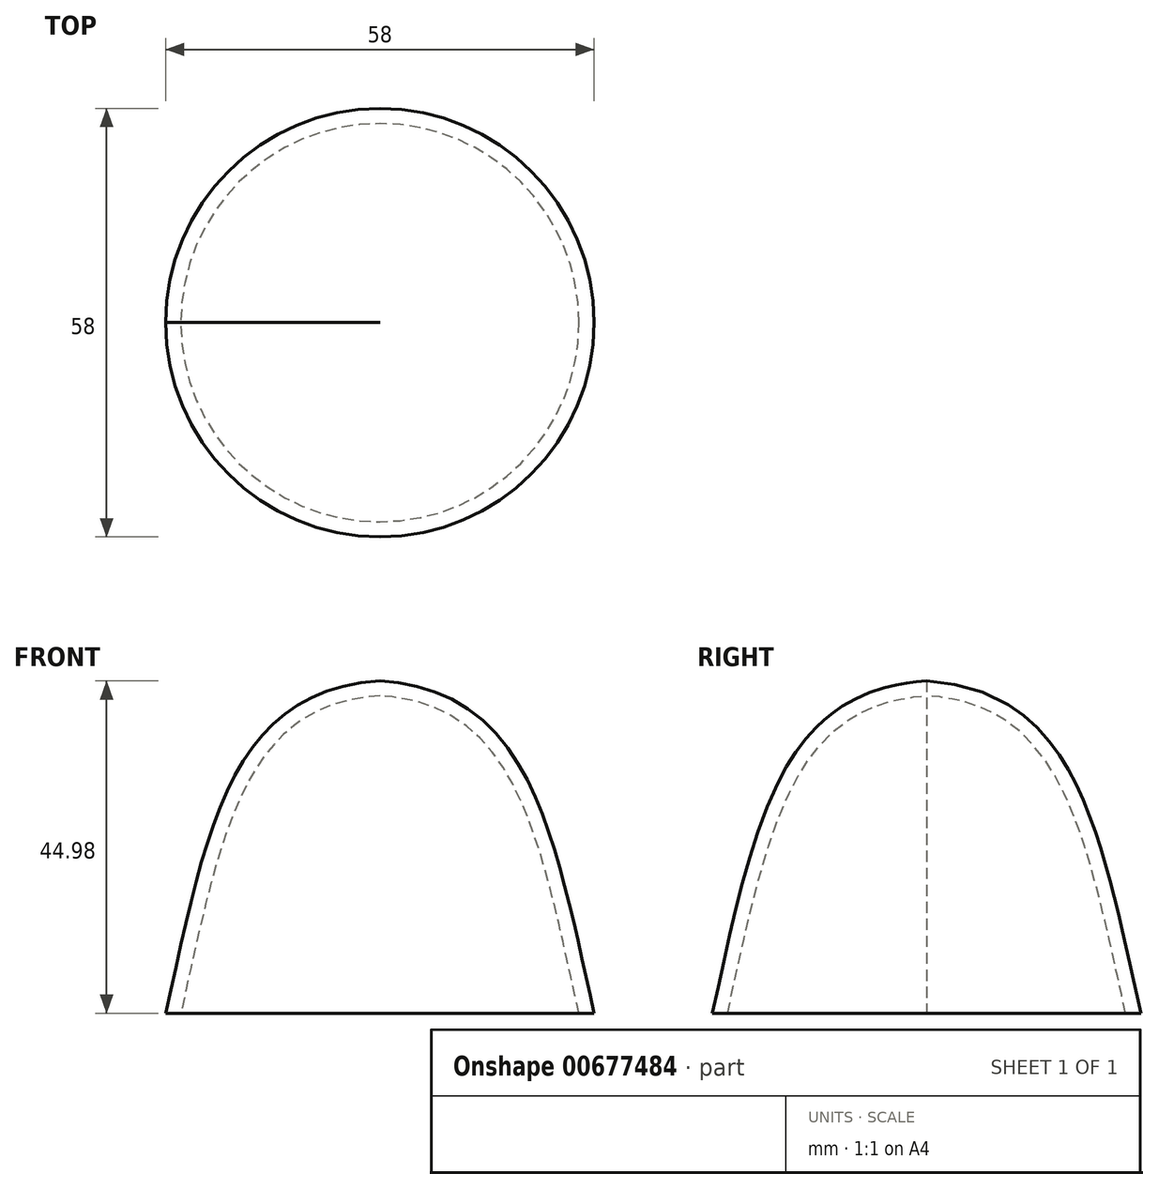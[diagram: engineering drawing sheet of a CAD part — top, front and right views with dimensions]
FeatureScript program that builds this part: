
annotation { "Feature Type Name" : "Feature", "Feature Type Description" : "" }
export const myFeature = defineFeature(function(context is Context, id is Id, definition is map)
    precondition{}
    {
        {
            var Q0;
            Q0=qCreatedBy(makeId("Front.planeOp"),FACE);
            var sketch = newSketch(context, id + "F0", { "sketchPlane" : qUnion([Q0])});
            skLineSegment(sketch, "E0", {"start": v(0, 0) * mm, "end": v(0, 45) * mm});
            skLineSegment(sketch, "E1", {"start": v(-29, 0.02) * mm, "end": v(0, 0) * mm});
            skFitSpline(sketch, "E2", {"points": [v(0, 45) * mm, v(-29, 0.02) * mm], "startDerivative": vector(-61.69, -3.83) * mm, "endDerivative": vector(-16.4, -72.98) * mm});
            skSolve(sketch);
        }
        {
            var Q0;
            Q0=makeQuery(id+"F0.imprint","IMPRINT",FACE,{"disambiguationData":[TD([[makeQuery(id+"F0.imprint","IMPRINT",EDGE,{"derivedFrom":sQuery(id+"F0.wireOp",EDGE,"E0")}),1.0]])]});
            var Q1;
            Q1=sQuery(id+"F0.wireOp",EDGE,"E0");
            var Q2;
            Q2=sQuery(id+"F0.wireOp",EDGE,"E1");
            var Q3;
            Q3=sQuery(id+"F0.wireOp",EDGE,"E2");
            var Q4;
            Q4=sQuery(id+"F0.wireOp",EDGE,"E0");
            revolve(context, id + "F1", {"entities" : qUnion([Q0]), "surfaceEntities" : qUnion([Q1, Q2, Q3]), "axis" : qUnion([Q4]), "revolveType" : RevolveType.FULL});
        }
        {
            var Q0;
            Q0=makeQuery(id+"F1.opRevolve","SWEPT_FACE",FACE,{"disambiguationData":[OSD([sQuery(id+"F0.wireOp",EDGE,"E1")])]});
            shell(context, id + "F2", {"entities" : qUnion([Q0]), "thickness" : 2 * mm});
        }
        {
            var Q0;
            Q0=qCreatedBy(makeId("Top.planeOp"),FACE);
            cPlane(context, id + "F3", {"entities" : qUnion([Q0]), "cplaneType" : CPlaneType.OFFSET, "offset" : 5 * mm, "width" : 150 * mm, "height" : 150 * mm});
        }
        {
            var Q0;
            Q0=qCreatedBy(makeId("Top.planeOp"),FACE);
            var sketch = newSketch(context, id + "F4", { "sketchPlane" : qUnion([Q0])});
            skCircle(sketch, "E3", {"center": v(0, 0) * mm, "radius": 27.5 * mm});
            skCircle(sketch, "E4", {"center": v(0, 0) * mm, "radius": 19 * mm});
            skSolve(sketch);
        }
        {
            var Q0;
            Q0=qCreatedBy(id+"F3.planeOp",FACE);
            var sketch = newSketch(context, id + "F5", { "sketchPlane" : qUnion([Q0])});
            skCircle(sketch, "E5.cCircle", {"center": v(-22.5, 0) * mm, "radius": 3 * mm, "construction": true});
            skLineSegment(sketch, "E5.0", {"start": v(-19.5, 1.73) * mm, "end": v(-19.5, -1.73) * mm});
            skLineSegment(sketch, "E5.1", {"start": v(-19.5, -1.73) * mm, "end": v(-22.5, -3.46) * mm});
            skLineSegment(sketch, "E5.2", {"start": v(-22.5, -3.46) * mm, "end": v(-25.5, -1.73) * mm});
            skLineSegment(sketch, "E5.3", {"start": v(-25.5, -1.73) * mm, "end": v(-25.5, 1.73) * mm});
            skLineSegment(sketch, "E5.4", {"start": v(-25.5, 1.73) * mm, "end": v(-22.5, 3.46) * mm});
            skLineSegment(sketch, "E5.5", {"start": v(-22.5, 3.46) * mm, "end": v(-19.5, 1.73) * mm});
            skPoint(sketch, "E5.0.midPoint", {"position": v(-19.5, 0) * mm});
            skCircle(sketch, "E6.cCircle", {"center": v(22.5, 0) * mm, "radius": 3 * mm, "construction": true});
            skLineSegment(sketch, "E6.0", {"start": v(25.5, 1.73) * mm, "end": v(25.5, -1.73) * mm});
            skLineSegment(sketch, "E6.1", {"start": v(25.5, -1.73) * mm, "end": v(22.5, -3.46) * mm});
            skLineSegment(sketch, "E6.2", {"start": v(22.5, -3.46) * mm, "end": v(19.5, -1.73) * mm});
            skLineSegment(sketch, "E6.3", {"start": v(19.5, -1.73) * mm, "end": v(19.5, 1.73) * mm});
            skLineSegment(sketch, "E6.4", {"start": v(19.5, 1.73) * mm, "end": v(22.5, 3.46) * mm});
            skLineSegment(sketch, "E6.5", {"start": v(22.5, 3.46) * mm, "end": v(25.5, 1.73) * mm});
            skPoint(sketch, "E6.0.midPoint", {"position": v(25.5, 0) * mm});
            skCircle(sketch, "E7", {"center": v(-22.5, 0) * mm, "radius": 1.65 * mm});
            skCircle(sketch, "E8", {"center": v(22.5, 0) * mm, "radius": 1.65 * mm});
            skSolve(sketch);
        }
        {
            var Q0;
            Q0=makeQuery(id+"FGVo4mOUeAnbViH_1.opExtrude","CAP_FACE",FACE,{"disambiguationData":[OSD([sQuery(id+"F4.wireOp",EDGE,"E3"),sQuery(id+"F4.wireOp",EDGE,"E4")])],"isStart":false});
            var sketch = newSketch(context, id + "F6", { "sketchPlane" : qUnion([Q0])});
            skCircle(sketch, "E9", {"center": v(-22.5, 0) * mm, "radius": 1.65 * mm});
            skCircle(sketch, "E10", {"center": v(22.5, 0) * mm, "radius": 1.65 * mm});
            skSolve(sketch);
        }
    });
